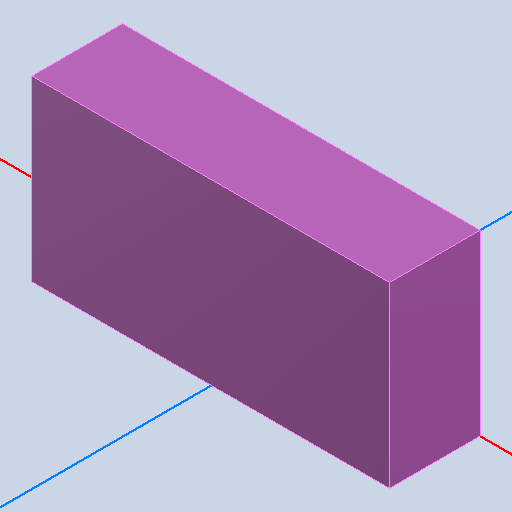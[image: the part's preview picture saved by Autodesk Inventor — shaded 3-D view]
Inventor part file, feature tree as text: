
AUTODESK INVENTOR PART (.ipt)
format: ipt  version: 2022 (Build 260153000, 153)  size: 92,672 bytes
history: native  units: mm
features: other x2, extrude x1
ambient origin geometry x8: Origin, YZ Plane, XZ Plane, XY Plane, X Axis, Y Axis, Z Axis, Center Point
bodies: Body1 (feature_tree)
feature tree (3):
  other  "Твердое тело1"
  extrude  "Выдавливание1"  Depth=1.0mm TaperAngle=0.0deg
  other  "R0805, R0805_10"
